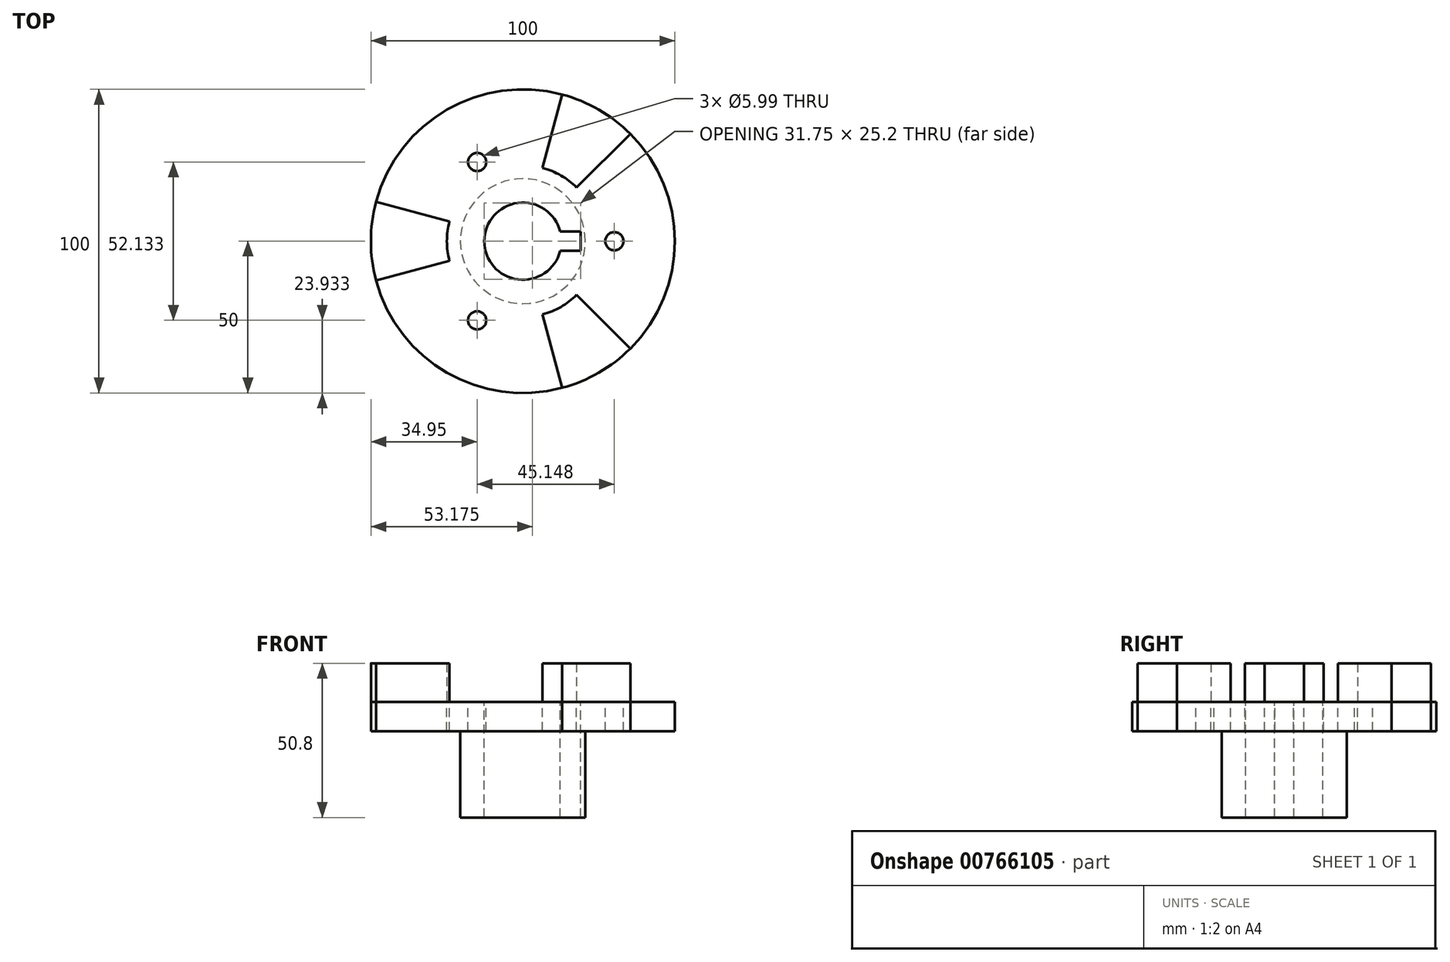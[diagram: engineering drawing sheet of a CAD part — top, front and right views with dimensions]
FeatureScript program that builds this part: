
annotation { "Feature Type Name" : "Feature", "Feature Type Description" : "" }
export const myFeature = defineFeature(function(context is Context, id is Id, definition is map)
    precondition{}
    {
        {
            var Q0;
            Q0=qCreatedBy(makeId("Top.planeOp"),FACE);
            var sketch = newSketch(context, id + "F0", { "sketchPlane" : qUnion([Q0])});
            skCircle(sketch, "E0", {"center": v(0, 0) * mm, "radius": 50 * mm});
            skArc(sketch, "E1", {"start": v(-24.15, 6.47) * mm, "mid": v(-25, 0) * mm, "end": v(-24.15, -6.47) * mm});
            skLineSegment(sketch, "E2", {"start": v(-24.15, 6.47) * mm, "end": v(-48.3, 12.94) * mm});
            skLineSegment(sketch, "E3", {"start": v(-24.15, -6.47) * mm, "end": v(-48.3, -12.94) * mm});
            skLineSegment(sketch, "E4", {"start": v(6.47, 24.15) * mm, "end": v(12.94, 48.3) * mm});
            skLineSegment(sketch, "E5", {"start": v(17.68, 17.68) * mm, "end": v(35.36, 35.36) * mm});
            skLineSegment(sketch, "E6", {"start": v(6.47, -24.15) * mm, "end": v(12.94, -48.3) * mm});
            skLineSegment(sketch, "E7", {"start": v(17.68, -17.68) * mm, "end": v(35.36, -35.36) * mm});
            skArc(sketch, "E8.trimOffspring", {"start": v(6.47, -24.15) * mm, "mid": v(12.5, -21.65) * mm, "end": v(17.68, -17.68) * mm});
            skArc(sketch, "E9.trimOffspring", {"start": v(17.68, 17.68) * mm, "mid": v(12.5, 21.65) * mm, "end": v(6.47, 24.15) * mm});
            skArc(sketch, "E10", {"start": v(12.3, 3.18) * mm, "mid": v(-12.7, 0) * mm, "end": v(12.3, -3.18) * mm});
            skLineSegment(sketch, "E11", {"start": v(19.05, 0) * mm, "end": v(19.05, 3.18) * mm});
            skLineSegment(sketch, "E12", {"start": v(19.05, 3.18) * mm, "end": v(12.3, 3.17) * mm});
            skLineSegment(sketch, "E13", {"start": v(19.05, 0) * mm, "end": v(19.05, -3.18) * mm});
            skLineSegment(sketch, "E14", {"start": v(19.05, -3.18) * mm, "end": v(12.3, -3.18) * mm});
            skCircle(sketch, "E15", {"center": v(-15.05, 26.07) * mm, "radius": 3 * mm});
            skCircle(sketch, "E16", {"center": v(-15.05, -26.07) * mm, "radius": 3 * mm});
            skCircle(sketch, "E17", {"center": v(30.1, 0) * mm, "radius": 3 * mm});
            skCircle(sketch, "E18", {"center": v(0, 0) * mm, "radius": 20.57 * mm});
            skSolve(sketch);
        }
        {
            var Q0;
            {var subQ4=sQuery(id+"F0.wireOp",EDGE,"E1");Q0=makeQuery(id+"F0.imprint","IMPRINT",FACE,{"disambiguationData":[TD([[makeQuery(id+"F0.imprint","IMPRINT",EDGE,{"derivedFrom":subQ4}),-1.0]])]});}
            var Q1;
            {var subQ0=sQuery(id+"F0.wireOp",EDGE,"E9.trimOffspring");Q1=makeQuery(id+"F0.imprint","IMPRINT",FACE,{"disambiguationData":[TD([[makeQuery(id+"F0.imprint","IMPRINT",EDGE,{"derivedFrom":subQ0}),-1.0]])]});}
            var Q2;
            {var subQ0=sQuery(id+"F0.wireOp",EDGE,"E8.trimOffspring");Q2=makeQuery(id+"F0.imprint","IMPRINT",FACE,{"disambiguationData":[TD([[makeQuery(id+"F0.imprint","IMPRINT",EDGE,{"derivedFrom":subQ0}),-1.0]])]});}
            extrude(context, id + "F1", {"entities" : qUnion([Q0, Q1, Q2]), "depth" : 12.7 * mm, "offsetDistance" : 25.4 * mm});
        }
        {
            var Q0;
            Q0=makeQuery(id+"F0.imprint","IMPRINT",FACE,{"disambiguationData":[TD([[makeQuery(id+"F0.imprint","IMPRINT",EDGE,{"derivedFrom":sQuery(id+"F0.wireOp",EDGE,"E1")}),1.0]])]});
            var Q1;
            Q1=makeQuery(id+"F0.imprint","IMPRINT",FACE,{"disambiguationData":[TD([[makeQuery(id+"F0.imprint","IMPRINT",EDGE,{"derivedFrom":sQuery(id+"F0.wireOp",EDGE,"E10")}),-1.0]])]});
            extrude(context, id + "F2", {"entities" : qUnion([Q0, Q1]), "depth" : -9.65 * mm, "offsetDistance" : 25.4 * mm});
        }
        {
            var Q0;
            Q0=makeQuery(id+"F1.opExtrude","CAP_FACE",FACE,{"disambiguationData":[OSD([sQuery(id+"F0.wireOp",EDGE,"E0"),sQuery(id+"F0.wireOp",EDGE,"E1"),sQuery(id+"F0.wireOp",EDGE,"E2"),sQuery(id+"F0.wireOp",EDGE,"E3")])],"isStart":true});
            var Q1;
            Q1=makeQuery(id+"F1.opExtrude","CAP_FACE",FACE,{"disambiguationData":[OSD([sQuery(id+"F0.wireOp",EDGE,"E0"),sQuery(id+"F0.wireOp",EDGE,"E4"),sQuery(id+"F0.wireOp",EDGE,"E5"),sQuery(id+"F0.wireOp",EDGE,"E9.trimOffspring")])],"isStart":true});
            var Q2;
            Q2=makeQuery(id+"F1.opExtrude","CAP_FACE",FACE,{"disambiguationData":[OSD([sQuery(id+"F0.wireOp",EDGE,"E0"),sQuery(id+"F0.wireOp",EDGE,"E6"),sQuery(id+"F0.wireOp",EDGE,"E7"),sQuery(id+"F0.wireOp",EDGE,"E8.trimOffspring")])],"isStart":true});
            extrude(context, id + "F3", {"entities" : qUnion([Q0, Q1, Q2]), "depth" : 9.65 * mm, "offsetDistance" : 25.4 * mm});
        }
        {
            var Q0;
            Q0=makeQuery(id+"F0.imprint","IMPRINT",FACE,{"disambiguationData":[TD([[makeQuery(id+"F0.imprint","IMPRINT",EDGE,{"derivedFrom":sQuery(id+"F0.wireOp",EDGE,"E10")}),-1.0]])]});
            extrude(context, id + "F4", {"entities" : qUnion([Q0]), "operationType" : NewBodyOperationType.ADD, "depth" : -38.1 * mm, "offsetDistance" : 25.4 * mm});
        }
    });
